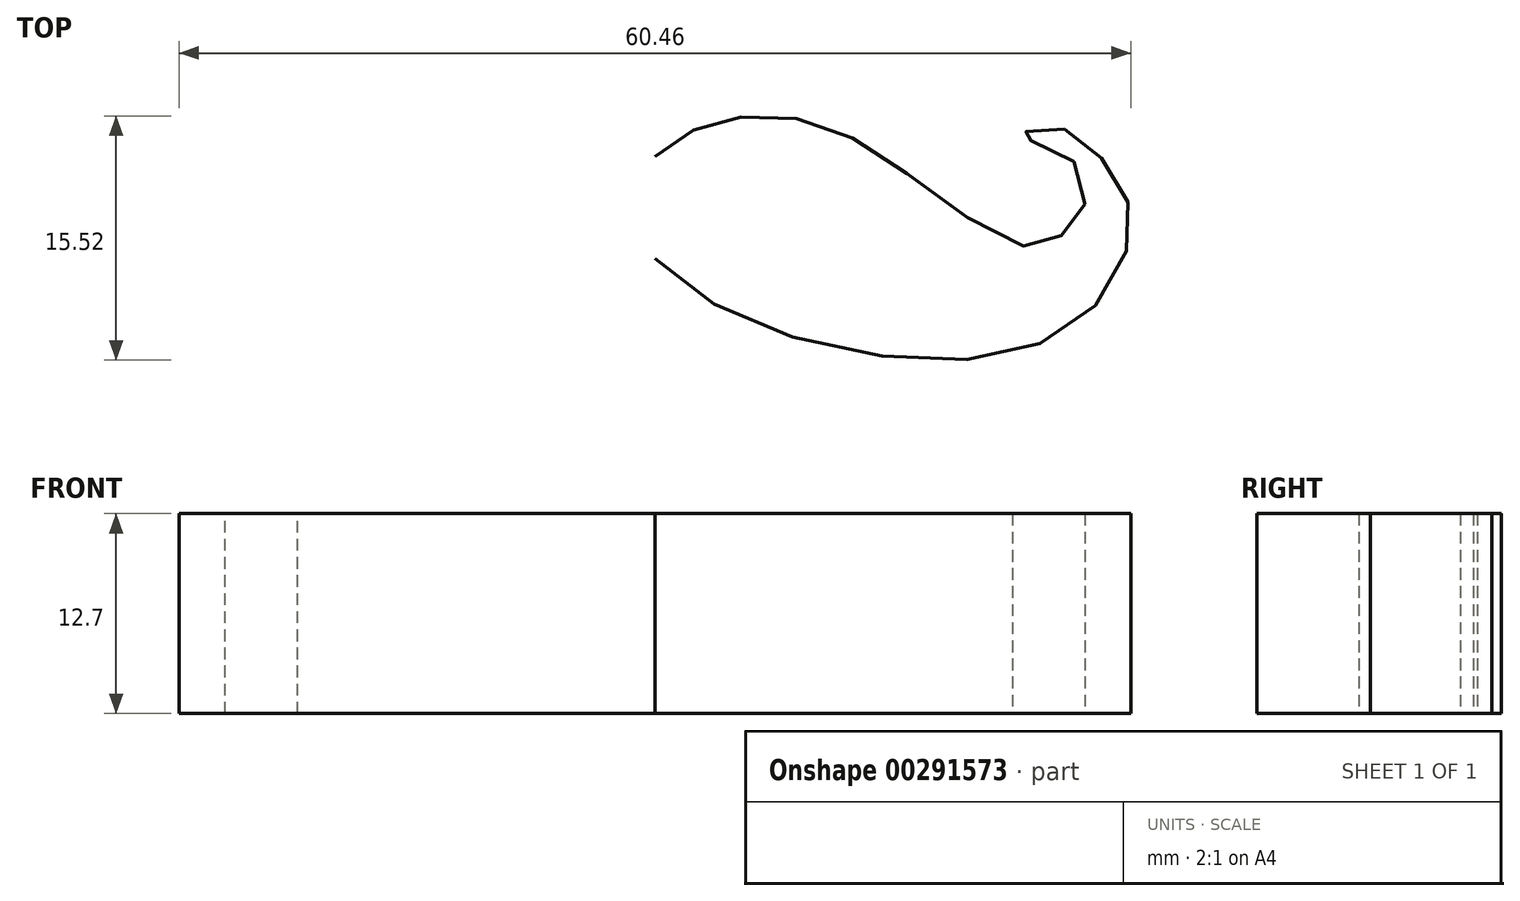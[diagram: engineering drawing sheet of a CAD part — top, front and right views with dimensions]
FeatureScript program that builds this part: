
annotation { "Feature Type Name" : "Feature", "Feature Type Description" : "" }
export const myFeature = defineFeature(function(context is Context, id is Id, definition is map)
    precondition{}
    {
        {
            var Q0;
            Q0=qCreatedBy(makeId("Top.planeOp"),FACE);
            var sketch = newSketch(context, id + "F0", { "sketchPlane" : qUnion([Q0])});
            skFitSpline(sketch, "E0", {"points": [v(0, -1.38) * mm, v(4.69, -4.8) * mm, v(12.44, -7.26) * mm, v(20.03, -7.78) * mm, v(25.32, -6.37) * mm, v(28.75, -3.47) * mm, v(30.16, 0) * mm, v(30.01, 2.27) * mm, v(28.75, 4.58) * mm, v(26.66, 6.44) * mm, v(25.47, 7.04) * mm, v(23.83, 6.81) * mm, v(22.71, 5.92) * mm, v(24.65, 6.14) * mm, v(26.59, 4.8) * mm, v(27.26, 2.94) * mm, v(27.03, 1.08) * mm, v(25.7, 0) * mm, v(24.28, -0.63) * mm, v(21.86, 0) * mm, v(17.25, 3.06) * mm, v(13.43, 5.78) * mm, v(9.92, 7.27) * mm, v(6.8, 7.67) * mm, v(3.75, 7.27) * mm, v(1.89, 6.44) * mm, v(0, 5.08) * mm], "startDerivative": vector(80.56, -69.68) * mm, "endDerivative": vector(-57.04, -43.78) * mm});
            skLineSegment(sketch, "E1", {"start": v(0, 5.08) * mm, "end": v(0, -1.38) * mm});
            skSolve(sketch);
        }
        {
            var Q0;
            Q0=makeQuery(id+"F0.imprint","IMPRINT",FACE,{"disambiguationData":[TD([[makeQuery(id+"F0.imprint","IMPRINT",EDGE,{"derivedFrom":sQuery(id+"F0.wireOp",EDGE,"E0")}),1.0]])]});
            extrude(context, id + "F1", {"entities" : qUnion([Q0]), "depth" : 12.7 * mm});
        }
        {
            var Q0;
            Q0=makeQuery(id+"F1.opExtrude","SWEPT_BODY",BODY,{"disambiguationData":[OSD([sQuery(id+"F0.wireOp",EDGE,"E0"),sQuery(id+"F0.wireOp",EDGE,"E1")])]});
            var Q1;
            Q1=qCreatedBy(makeId("Right.planeOp"),FACE);
            mirror(context, id + "F2", {"operationType" : NewBodyOperationType.ADD, "entities" : qUnion([Q0]), "mirrorPlane" : qUnion([Q1])});
        }
    });
